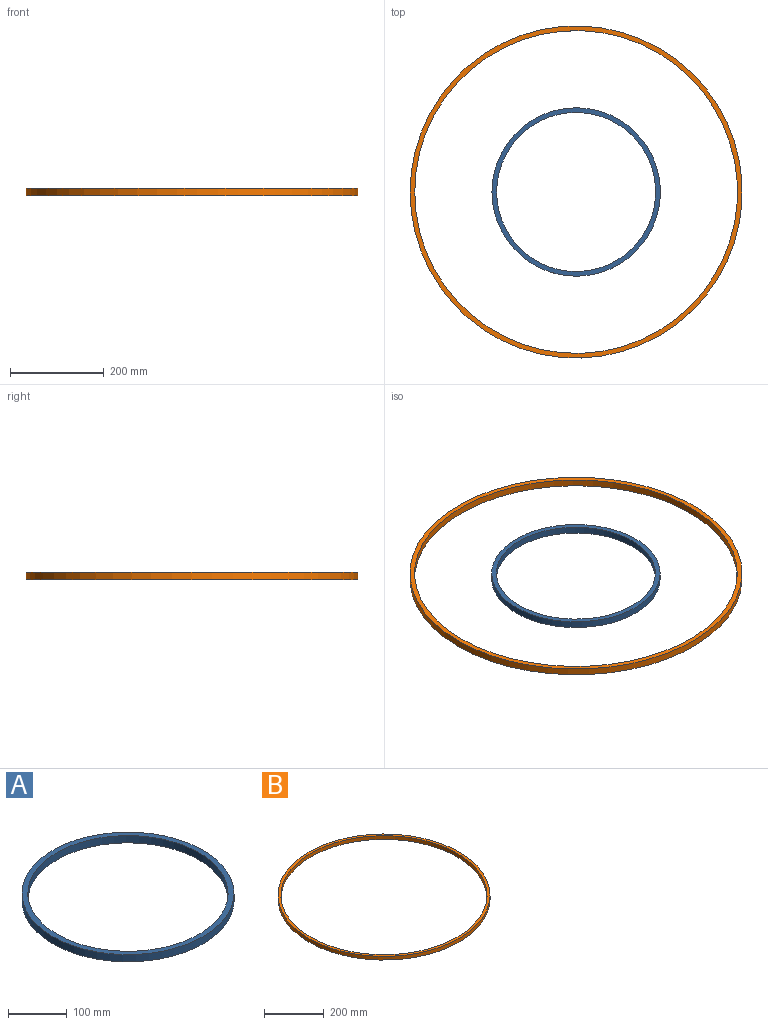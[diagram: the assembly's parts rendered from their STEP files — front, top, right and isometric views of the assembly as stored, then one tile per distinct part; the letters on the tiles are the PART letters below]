
ASSEMBLY  parts=2 mates=1
PART A: 4 faces, bbox 360x360x15 mm
  f0: cylinder r=170mm len=340mm, axis (0,0,-1), area 16022.1mm2, adj f1,f3
  f1: plane 360x360mm, normal (0,0,1), area 10995.6mm2, adj f0,f2
  f2: cylinder r=180mm len=360mm, axis (0,0,-1), area 16964.6mm2, adj f1,f3
  f3: plane 360x360mm, normal (0,0,-1), area 10995.6mm2, adj f0,f2
PART B: 4 faces, bbox 710x710x15 mm
  f0: cylinder r=345mm len=690mm, axis (0,0,-1), area 32515.5mm2, adj f1,f3
  f1: plane 710x710mm, normal (0,0,1), area 21991.1mm2, adj f0,f2
  f2: cylinder r=355mm len=710mm, axis (0,0,-1), area 33458mm2, adj f1,f3
  f3: plane 710x710mm, normal (0,0,-1), area 21991.1mm2, adj f0,f2
PLACE A t=(-7.81,9.27,-7.23)mm
PLACE B t=(-7.81,9.27,-7.23)mm
MATE fastened A.f0 <-> B.f0  axis (0,0,1) through (-7.81,9.27,0.27)mm
